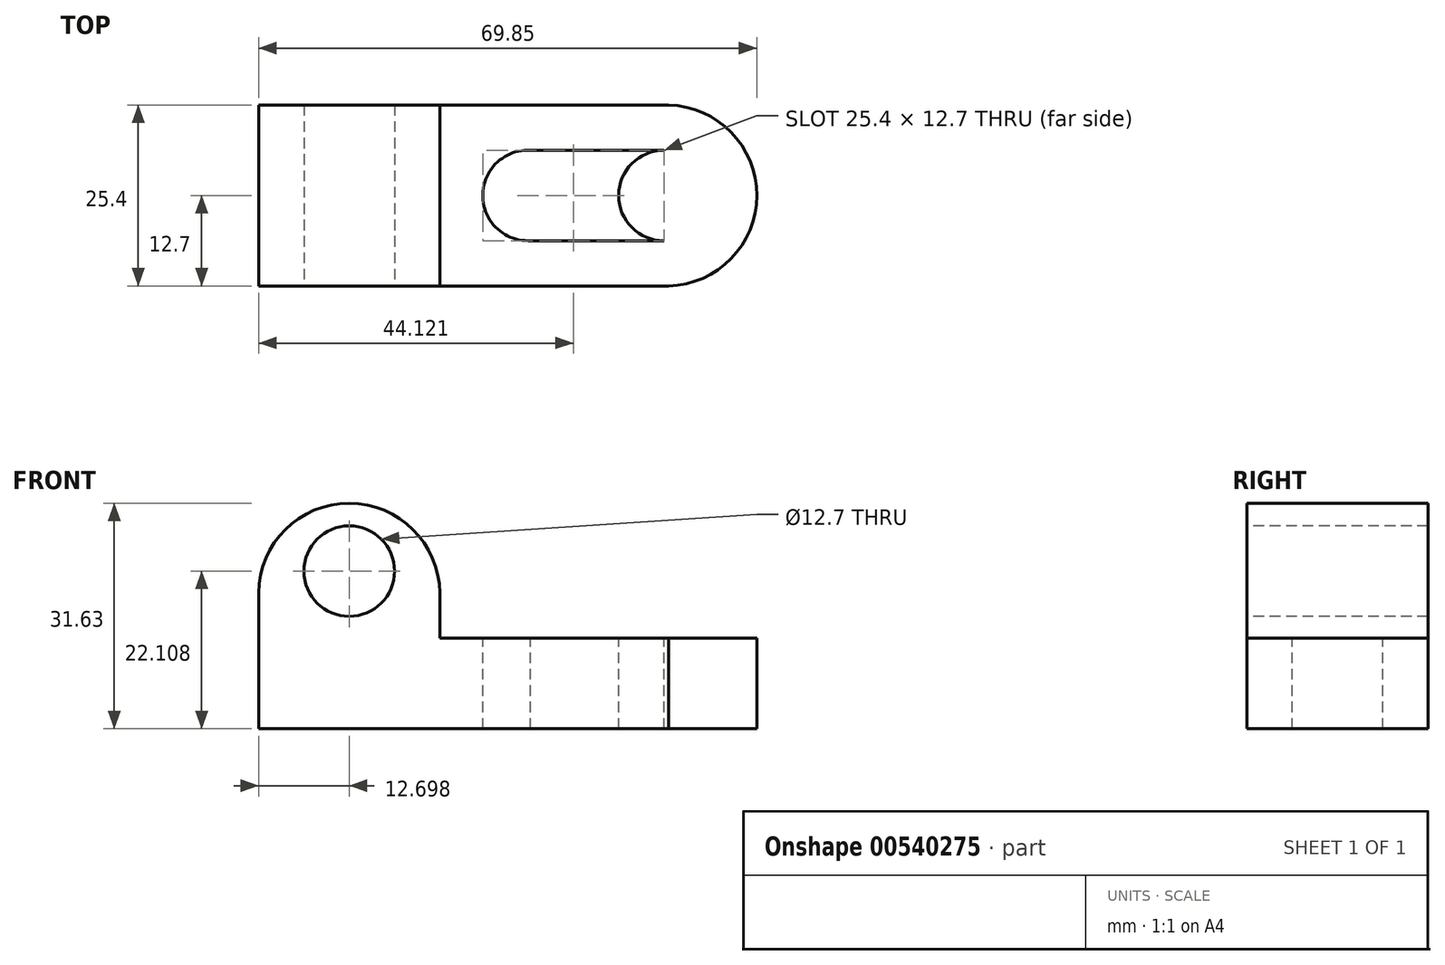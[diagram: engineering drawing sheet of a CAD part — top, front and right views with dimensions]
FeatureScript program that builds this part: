
annotation { "Feature Type Name" : "Feature", "Feature Type Description" : "" }
export const myFeature = defineFeature(function(context is Context, id is Id, definition is map)
    precondition{}
    {
        {
            var Q0;
            Q0=qCreatedBy(makeId("Front.planeOp"),FACE);
            var sketch = newSketch(context, id + "F0", { "sketchPlane" : qUnion([Q0])});
            skLineSegment(sketch, "E0", {"start": v(-56.82, 31.75) * mm, "end": v(-56.82, 0) * mm});
            skLineSegment(sketch, "E1", {"start": v(-56.82, 0) * mm, "end": v(13.03, 0) * mm});
            skLineSegment(sketch, "E2", {"start": v(13.03, 0) * mm, "end": v(13.03, 12.7) * mm});
            skLineSegment(sketch, "E3", {"start": v(13.03, 12.7) * mm, "end": v(-31.42, 12.7) * mm});
            skLineSegment(sketch, "E4", {"start": v(-31.42, 12.7) * mm, "end": v(-31.42, 31.52) * mm});
            skLineSegment(sketch, "E5", {"start": v(-31.42, 31.52) * mm, "end": v(-56.82, 31.75) * mm});
            skSolve(sketch);
        }
        {
            var Q0;
            Q0 = qSketchRegion(id + "F0", true);
            extrude(context, id + "F1", {"entities" : qUnion([Q0]), "depth" : 25.4 * mm, "offsetDistance" : 25.4 * mm});
        }
        {
            var Q0;
            Q0=makeQuery(id+"F1.opExtrude","CAP_FACE",FACE,{"disambiguationData":[OSD([sQuery(id+"F0.wireOp",EDGE,"E0"),sQuery(id+"F0.wireOp",EDGE,"E1"),sQuery(id+"F0.wireOp",EDGE,"E2"),sQuery(id+"F0.wireOp",EDGE,"E3"),sQuery(id+"F0.wireOp",EDGE,"E4"),sQuery(id+"F0.wireOp",EDGE,"E5")])],"isStart":false});
            var sketch = newSketch(context, id + "F2", { "sketchPlane" : qUnion([Q0])});
            skCircle(sketch, "E6", {"center": v(-44.12, 22.1) * mm, "radius": 6.35 * mm});
            skSolve(sketch);
        }
        {
            var Q0;
            Q0=makeQuery(id+"F2.imprint","IMPRINT",FACE,{"disambiguationData":[TD([[makeQuery(id+"F2.imprint","IMPRINT",EDGE,{"derivedFrom":sQuery(id+"F2.wireOp",EDGE,"E6")}),1.0]])]});
            extrude(context, id + "F3", {"entities" : qUnion([Q0]), "operationType" : NewBodyOperationType.REMOVE, "endBound" : BoundingType.THROUGH_ALL, "oppositeDirection" : true, "depth" : 25.4 * mm, "offsetDistance" : 25.4 * mm});
        }
        {
            var Q0;
            Q0=makeQuery(id+"F1.opExtrude","CAP_FACE",FACE,{"disambiguationData":[OSD([sQuery(id+"F0.wireOp",EDGE,"E0"),sQuery(id+"F0.wireOp",EDGE,"E1"),sQuery(id+"F0.wireOp",EDGE,"E2"),sQuery(id+"F0.wireOp",EDGE,"E3"),sQuery(id+"F0.wireOp",EDGE,"E4"),sQuery(id+"F0.wireOp",EDGE,"E5")])],"isStart":false});
            var sketch = newSketch(context, id + "F4", { "sketchPlane" : qUnion([Q0])});
            skArc(sketch, "E7", {"start": v(-31.42, 18.82) * mm, "mid": v(-44, 31.63) * mm, "end": v(-56.82, 19.05) * mm});
            skSolve(sketch);
        }
        {
            var Q0;
            Q0 = qSketchRegion(id + "F4", true);
            var Q1;
            {var subQ0=sQuery(id+"F4.wireOp",EDGE,"E7");var subQ1=makeQuery(id+"F1.opExtrude","CAP_EDGE",EDGE,{"disambiguationData":[OSD([sQuery(id+"F0.wireOp",EDGE,"E0")])],"isStart":false});var subQ2=makeQuery(id+"F4.imprint","INTERSECT",VERTEX,{"derivedFrom":[subQ1,subQ0]});Q1=makeQuery(id+"F4.imprint","IMPRINT",FACE,{"disambiguationData":[TD([[makeQuery(id+"F4.imprint","IMPRINT",EDGE,{"disambiguationData":[TD([[subQ2,1.0]])],"derivedFrom":subQ0}),-1.0]])]});}
            var Q2;
            {var subQ0=sQuery(id+"F4.wireOp",EDGE,"E7");var subQ1=makeQuery(id+"F1.opExtrude","CAP_EDGE",EDGE,{"disambiguationData":[OSD([sQuery(id+"F0.wireOp",EDGE,"E4")])],"isStart":false});var subQ2=makeQuery(id+"F4.imprint","INTERSECT",VERTEX,{"disambiguationData":[OD(1.0)],"derivedFrom":[subQ1,subQ0]});Q2=makeQuery(id+"F4.imprint","IMPRINT",FACE,{"disambiguationData":[TD([[makeQuery(id+"F4.imprint","IMPRINT",EDGE,{"disambiguationData":[TD([[subQ2,-1.0]])],"derivedFrom":subQ0}),-1.0]])]});}
            extrude(context, id + "F5", {"entities" : qUnion([Q0, Q1, Q2]), "operationType" : NewBodyOperationType.REMOVE, "oppositeDirection" : true, "depth" : 25.4 * mm, "offsetDistance" : 25.4 * mm});
        }
        {
            var Q0;
            Q0=makeQuery(id+"F1.opExtrude","SWEPT_FACE",FACE,{"disambiguationData":[OSD([sQuery(id+"F0.wireOp",EDGE,"E3")])]});
            var sketch = newSketch(context, id + "F6", { "sketchPlane" : qUnion([Q0])});
            skCircle(sketch, "E8", {"center": v(-19.05, -12.7) * mm, "radius": 6.35 * mm});
            skCircle(sketch, "E9", {"center": v(0, -12.7) * mm, "radius": 6.35 * mm});
            skLineSegment(sketch, "E10", {"start": v(-18.68, -6.36) * mm, "end": v(0, -6.35) * mm});
            skLineSegment(sketch, "E11", {"start": v(-19.05, -19.05) * mm, "end": v(0, -19.05) * mm});
            skSolve(sketch);
        }
        {
            var Q0;
            {var subQ0=sQuery(id+"F6.wireOp",EDGE,"E9");var subQ2=makeQuery(id+"F6.imprint","IMPRINT",VERTEX,{"derivedFrom":subQ0});Q0=makeQuery(id+"F6.imprint","IMPRINT",FACE,{"disambiguationData":[TD([[makeQuery(id+"F6.imprint","IMPRINT",EDGE,{"disambiguationData":[TD([[subQ2,-1.0]])],"derivedFrom":subQ0}),1.0]])]});}
            var Q1;
            {var subQ0=sQuery(id+"F6.wireOp",EDGE,"E10");Q1=makeQuery(id+"F6.imprint","IMPRINT",FACE,{"disambiguationData":[TD([[makeQuery(id+"F6.imprint","IMPRINT",EDGE,{"derivedFrom":subQ0}),-1.0]])]});}
            var Q2;
            {var subQ0=sQuery(id+"F6.wireOp",EDGE,"E8");var subQ1=makeQuery(id+"F6.imprint","INTERSECT",VERTEX,{"derivedFrom":[subQ0,sQuery(id+"F6.wireOp",EDGE,"E10")]});Q2=makeQuery(id+"F6.imprint","IMPRINT",FACE,{"disambiguationData":[TD([[makeQuery(id+"F6.imprint","IMPRINT",EDGE,{"disambiguationData":[TD([[subQ1,-1.0]])],"derivedFrom":subQ0}),1.0]])]});}
            extrude(context, id + "F7", {"entities" : qUnion([Q0, Q1, Q2]), "operationType" : NewBodyOperationType.REMOVE, "endBound" : BoundingType.THROUGH_ALL, "oppositeDirection" : true, "depth" : 25.4 * mm, "offsetDistance" : 25.4 * mm});
        }
        {
            var Q0;
            Q0=makeQuery(id+"F1.opExtrude","SWEPT_FACE",FACE,{"disambiguationData":[OSD([sQuery(id+"F0.wireOp",EDGE,"E3")])]});
            var sketch = newSketch(context, id + "F8", { "sketchPlane" : qUnion([Q0])});
            skArc(sketch, "E12", {"start": v(0, -25.4) * mm, "mid": v(13.03, -12.7) * mm, "end": v(0, 0) * mm});
            skSolve(sketch);
        }
        {
            var Q0;
            Q0 = qSketchRegion(id + "F8", true);
            var Q1;
            {var subQ0=sQuery(id+"F8.wireOp",EDGE,"E12");var subQ1=sQuery(id+"F0.wireOp",EDGE,"E3");var subQ4=makeQuery(id+"F1.opExtrude","CAP_EDGE",EDGE,{"disambiguationData":[OSD([subQ1])],"isStart":true});var subQ5=makeQuery(id+"F8.imprint","INTERSECT",VERTEX,{"disambiguationData":[OD(1.0)],"derivedFrom":[subQ4,subQ0]});Q1=makeQuery(id+"F8.imprint","IMPRINT",FACE,{"disambiguationData":[TD([[makeQuery(id+"F8.imprint","IMPRINT",EDGE,{"disambiguationData":[TD([[subQ5,1.0]])],"derivedFrom":subQ0}),-1.0]])]});}
            var Q2;
            {var subQ0=sQuery(id+"F8.wireOp",EDGE,"E12");var subQ1=sQuery(id+"F0.wireOp",EDGE,"E3");var subQ2=makeQuery(id+"F1.opExtrude","CAP_EDGE",EDGE,{"disambiguationData":[OSD([subQ1])],"isStart":false});var subQ3=makeQuery(id+"F8.imprint","INTERSECT",VERTEX,{"disambiguationData":[OD(1.0)],"derivedFrom":[subQ2,subQ0]});Q2=makeQuery(id+"F8.imprint","IMPRINT",FACE,{"disambiguationData":[TD([[makeQuery(id+"F8.imprint","IMPRINT",EDGE,{"disambiguationData":[TD([[subQ3,-1.0]])],"derivedFrom":subQ0}),-1.0]])]});}
            extrude(context, id + "F9", {"entities" : qUnion([Q0, Q1, Q2]), "operationType" : NewBodyOperationType.REMOVE, "endBound" : BoundingType.THROUGH_ALL, "oppositeDirection" : true, "depth" : 25.4 * mm, "offsetDistance" : 25.4 * mm});
        }
    });
